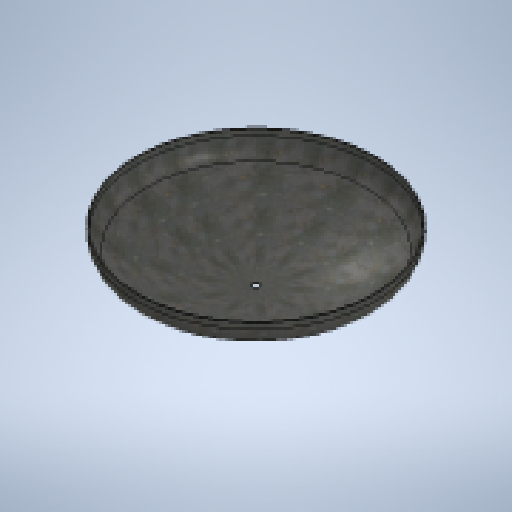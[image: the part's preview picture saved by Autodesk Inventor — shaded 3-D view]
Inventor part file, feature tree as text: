
AUTODESK INVENTOR PART (.ipt)
format: ipt  version: 2025.1 (Build 291241020, 241B)  size: 216,064 bytes
history: native  units: mm
features: sketch x2, revolve x1, extrude x1
ambient origin geometry x8: Origin, YZ Plane, XZ Plane, XY Plane, X Axis, Y Axis, Z Axis, Center Point
bodies: Solid1 (feature_tree)
feature tree (4):
  revolve  "Revolution1"  [1 undecoded]
  extrude  "Extrusion1"  Depth=1084.414286mm
  sketch  "Sketch1"  dims[d0=100.0mm d1=30.0mm]
  sketch  "Sketch2"  dims[d3=1084.414286mm d6=6.0mm d7=90.0deg d8=33.5mm d9=0.0mm d10=0.0mm d11=1200.0mm d12=270.0mm]
note: 1 required parameter value undecoded (feature->parameter linkage not recoverable at this tier; creation-order binding heuristic only, values carry confidence <= 0.55)
